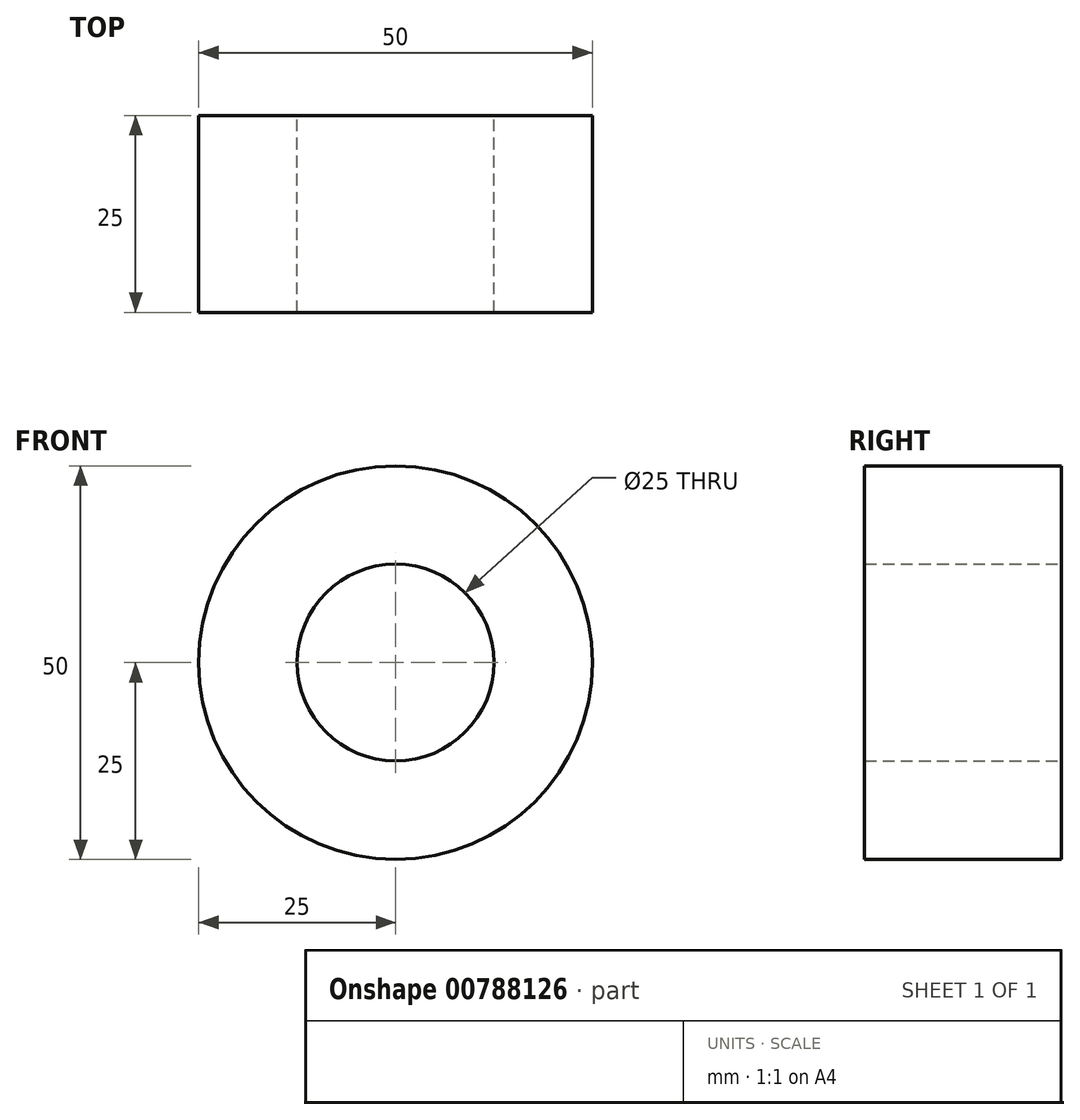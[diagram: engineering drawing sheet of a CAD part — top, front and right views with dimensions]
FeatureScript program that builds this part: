
annotation { "Feature Type Name" : "Feature", "Feature Type Description" : "" }
export const myFeature = defineFeature(function(context is Context, id is Id, definition is map)
    precondition{}
    {
        {
            var Q0;
            Q0=qCreatedBy(makeId("Front.planeOp"),FACE);
            var sketch = newSketch(context, id + "F0", { "sketchPlane" : qUnion([Q0])});
            skCircle(sketch, "E0", {"center": v(0, 0) * mm, "radius": 25 * mm});
            skCircle(sketch, "E1", {"center": v(0, 0) * mm, "radius": 12.5 * mm});
            skSolve(sketch);
        }
        {
            var Q0;
            Q0 = qSketchRegion(id + "F0", true);
            extrude(context, id + "F1", {"entities" : qUnion([Q0]), "depth" : 25 * mm, "offsetDistance" : 25 * mm});
        }
    });
